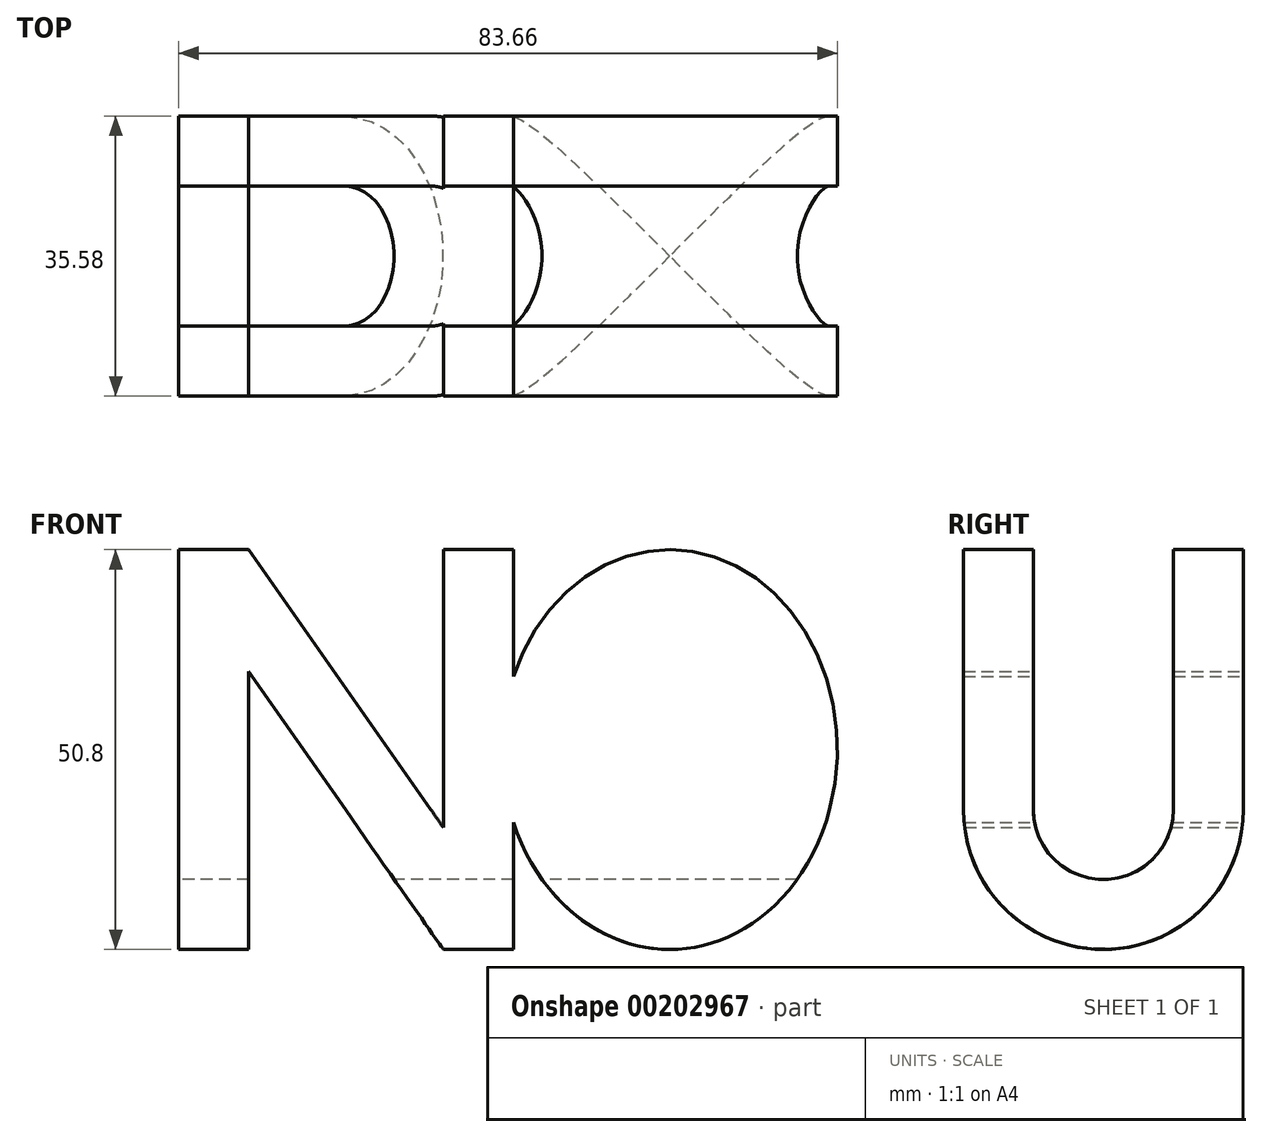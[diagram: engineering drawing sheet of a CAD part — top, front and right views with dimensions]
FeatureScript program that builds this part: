
annotation { "Feature Type Name" : "Feature", "Feature Type Description" : "" }
export const myFeature = defineFeature(function(context is Context, id is Id, definition is map)
    precondition{}
    {
        {
            var Q0;
            Q0=qCreatedBy(makeId("Front.planeOp"),FACE);
            var sketch = newSketch(context, id + "F0", { "sketchPlane" : qUnion([Q0])});
            skEllipse(sketch, "E0", {"center": v(20.52, 0) * mm, "majorRadius": 21.31 * mm, "minorRadius": 25.4 * mm, "majorAxis": v(1, 0)});
            skLineSegment(sketch, "E1", {"start": v(0.67, 25.4) * mm, "end": v(20.52, 25.4) * mm, "construction": true});
            skLineSegment(sketch, "E2", {"start": v(20.52, 25.4) * mm, "end": v(41.83, 0) * mm, "construction": true});
            skFitSpline(sketch, "E3.0", {"points": [v(21.58, 16.47) * mm, v(20.52, 16.53) * mm, v(19.45, 16.47) * mm, v(18.4, 16.28) * mm, v(17.35, 15.97) * mm, v(15.94, 15.37) * mm, v(14.55, 14.5) * mm, v(13.21, 13.31) * mm, v(12.25, 12.27) * mm, v(11.34, 11.08) * mm, v(10.53, 9.77) * mm, v(9.8, 8.34) * mm, v(9.2, 6.82) * mm, v(8.72, 5.2) * mm, v(8.36, 3.52) * mm, v(8.18, 2.07) * mm, v(8.1, 0.9) * mm, v(8.09, 0) * mm, v(8.1, -0.9) * mm, v(8.18, -2.07) * mm, v(8.36, -3.52) * mm, v(8.72, -5.2) * mm, v(9.2, -6.82) * mm, v(9.8, -8.34) * mm, v(10.53, -9.77) * mm, v(11.34, -11.08) * mm, v(12.25, -12.27) * mm, v(13.21, -13.31) * mm, v(14.55, -14.5) * mm, v(15.94, -15.37) * mm, v(17.35, -15.97) * mm, v(18.4, -16.28) * mm, v(19.45, -16.47) * mm, v(20.52, -16.53) * mm, v(21.58, -16.47) * mm, v(22.63, -16.28) * mm, v(23.69, -15.97) * mm, v(25.09, -15.37) * mm, v(26.48, -14.5) * mm, v(27.82, -13.31) * mm, v(28.79, -12.27) * mm, v(29.7, -11.08) * mm, v(30.5, -9.77) * mm, v(31.22, -8.34) * mm, v(31.83, -6.82) * mm, v(32.32, -5.2) * mm, v(32.67, -3.52) * mm, v(32.85, -2.07) * mm, v(32.93, -0.9) * mm, v(32.95, 0) * mm, v(32.93, 0.9) * mm, v(32.85, 2.07) * mm, v(32.67, 3.52) * mm, v(32.32, 5.2) * mm, v(31.83, 6.82) * mm, v(31.22, 8.34) * mm, v(30.5, 9.77) * mm, v(29.7, 11.08) * mm, v(28.79, 12.27) * mm, v(27.82, 13.31) * mm, v(26.48, 14.5) * mm, v(25.09, 15.37) * mm, v(23.69, 15.97) * mm, v(22.63, 16.28) * mm, v(21.58, 16.47) * mm, v(20.52, 16.53) * mm, v(19.45, 16.47) * mm, v(21.58, 16.47) * mm]});
            skLineSegment(sketch, "E4", {"start": v(20.52, 25.4) * mm, "end": v(20.52, 16.51) * mm, "construction": true});
            skLineSegment(sketch, "E5", {"start": v(-41.83, -25.4) * mm, "end": v(-41.83, 25.4) * mm});
            skLineSegment(sketch, "E6", {"start": v(-41.83, 25.4) * mm, "end": v(-32.94, 25.4) * mm});
            skLineSegment(sketch, "E7", {"start": v(-32.94, 25.4) * mm, "end": v(-8.22, -9.9) * mm});
            skLineSegment(sketch, "E8", {"start": v(-8.22, -9.9) * mm, "end": v(-8.22, 25.4) * mm});
            skLineSegment(sketch, "E9", {"start": v(-8.22, 25.4) * mm, "end": v(0.67, 25.4) * mm});
            skLineSegment(sketch, "E10", {"start": v(0.67, 25.4) * mm, "end": v(0.67, -25.4) * mm});
            skLineSegment(sketch, "E11", {"start": v(0.67, -25.4) * mm, "end": v(-8.22, -25.4) * mm});
            skLineSegment(sketch, "E12", {"start": v(-8.22, -25.4) * mm, "end": v(-32.94, 9.9) * mm});
            skLineSegment(sketch, "E13", {"start": v(-32.94, 9.9) * mm, "end": v(-32.94, -25.4) * mm});
            skLineSegment(sketch, "E14", {"start": v(-32.94, -25.4) * mm, "end": v(-41.83, -25.4) * mm});
            skLineSegment(sketch, "E15", {"start": v(-25.66, 15) * mm, "end": v(-32.94, 9.9) * mm, "construction": true});
            skPoint(sketch, "E16", {"position": v(0.67, 0) * mm});
            skLineSegment(sketch, "E17", {"start": v(-41.83, -25.4) * mm, "end": v(41.83, 25.4) * mm, "construction": true});
            skPoint(sketch, "E18", {"position": v(0.67, 9.26) * mm});
            skLineSegment(sketch, "E19", {"start": v(0.67, 9.26) * mm, "end": v(20.52, 0) * mm, "construction": true});
            skSolve(sketch);
        }
        {
            var Q0;
            Q0 = qSketchRegion(id + "F0", true);
            extrude(context, id + "F1", {"entities" : qUnion([Q0]), "endBound" : BoundingType.SYMMETRIC, "depth" : 101.6 * mm});
        }
        {
            var Q0;
            Q0=qCreatedBy(makeId("Right.planeOp"),FACE);
            var sketch = newSketch(context, id + "F2", { "sketchPlane" : qUnion([Q0])});
            skLineSegment(sketch, "E20", {"start": v(-17.79, 25.4) * mm, "end": v(-17.79, -7.61) * mm});
            skArc(sketch, "E21", {"start": v(-17.79, -7.61) * mm, "mid": v(0, -25.4) * mm, "end": v(17.79, -7.61) * mm});
            skLineSegment(sketch, "E22", {"start": v(17.79, -7.61) * mm, "end": v(17.79, 25.4) * mm});
            skLineSegment(sketch, "E23.0", {"start": v(8.9, -7.61) * mm, "end": v(8.9, 25.4) * mm});
            skArc(sketch, "E23.1", {"start": v(-8.9, -7.61) * mm, "mid": v(0, -16.5) * mm, "end": v(8.9, -7.61) * mm});
            skLineSegment(sketch, "E23.2", {"start": v(-8.9, 25.4) * mm, "end": v(-8.9, -7.61) * mm});
            skLineSegment(sketch, "E24", {"start": v(17.79, 25.4) * mm, "end": v(8.9, 25.4) * mm});
            skLineSegment(sketch, "E25", {"start": v(-8.9, 25.4) * mm, "end": v(-17.79, 25.4) * mm});
            skLineSegment(sketch, "E26", {"start": v(-17.79, 25.4) * mm, "end": v(17.79, -25.4) * mm, "construction": true});
            skSolve(sketch);
        }
        {
            var Q0;
            Q0 = qSketchRegion(id + "F2", true);
            extrude(context, id + "F3", {"entities" : qUnion([Q0]), "operationType" : NewBodyOperationType.INTERSECT, "endBound" : BoundingType.THROUGH_ALL, "depth" : 25.4 * mm, "hasSecondDirection" : true, "secondDirectionBound" : SecondDirectionBoundingType.THROUGH_ALL, "secondDirectionOppositeDirection" : true, "secondDirectionDepth" : 25.4 * mm});
        }
    });
